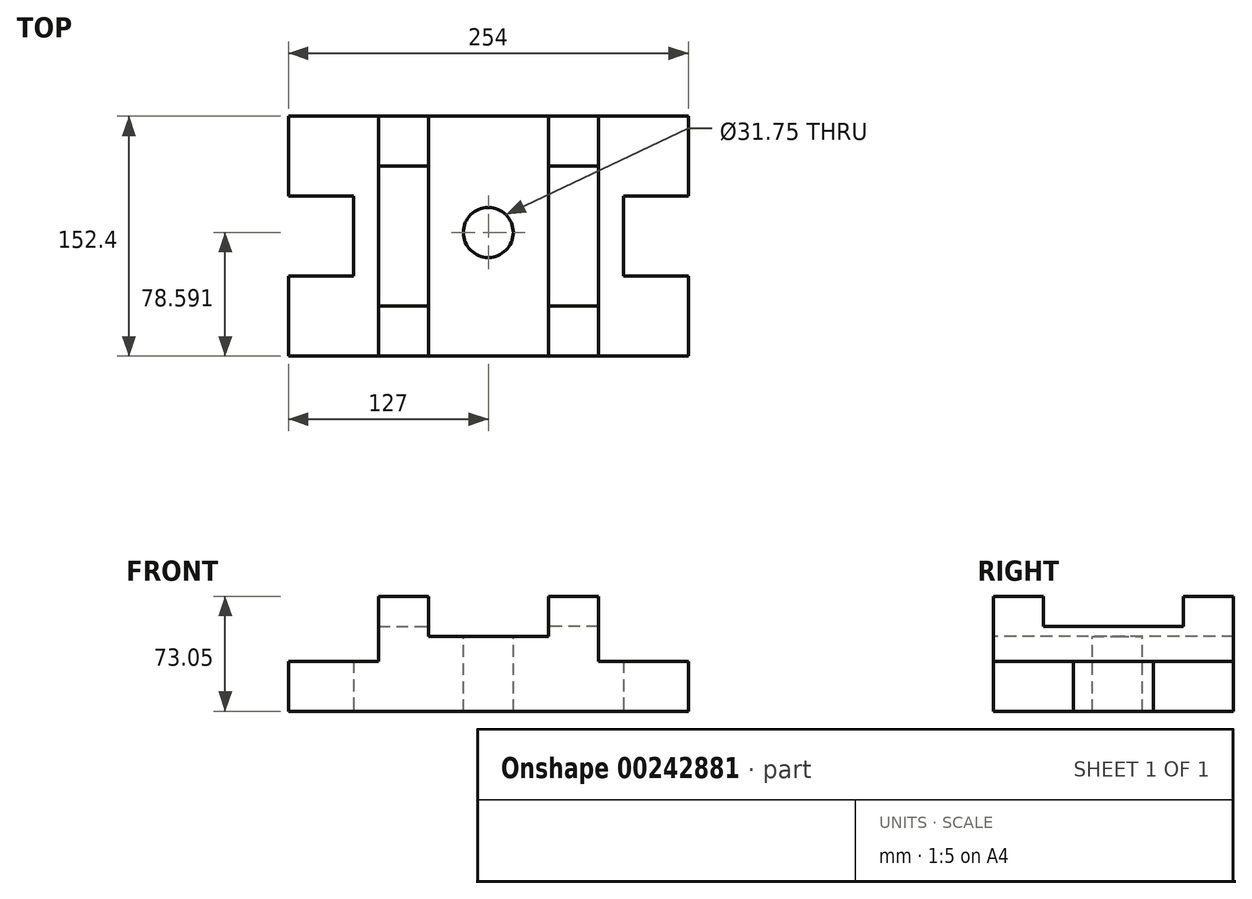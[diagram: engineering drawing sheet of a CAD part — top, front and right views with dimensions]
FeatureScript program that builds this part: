
annotation { "Feature Type Name" : "Feature", "Feature Type Description" : "" }
export const myFeature = defineFeature(function(context is Context, id is Id, definition is map)
    precondition{}
    {
        {
            var Q0;
            Q0=qCreatedBy(makeId("Top.planeOp"),FACE);
            var sketch = newSketch(context, id + "F0", { "sketchPlane" : qUnion([Q0])});
            skLineSegment(sketch, "E0.bottom", {"start": v(127, -76.2) * mm, "end": v(-127, -76.2) * mm});
            skLineSegment(sketch, "E0.top", {"start": v(127, 76.2) * mm, "end": v(-127, 76.2) * mm});
            skLineSegment(sketch, "E0.left", {"start": v(127, -76.2) * mm, "end": v(127, -25.4) * mm});
            skLineSegment(sketch, "E0.right", {"start": v(-127, -76.2) * mm, "end": v(-127, -25.4) * mm});
            skPoint(sketch, "E0.middle", {"position": v(0, 0) * mm});
            skLineSegment(sketch, "E1", {"start": v(127, 76.2) * mm, "end": v(127, 25.4) * mm});
            skLineSegment(sketch, "E2", {"start": v(127, 25.4) * mm, "end": v(85.72, 25.4) * mm});
            skLineSegment(sketch, "E3", {"start": v(127, -25.4) * mm, "end": v(85.72, -25.4) * mm});
            skLineSegment(sketch, "E4", {"start": v(85.72, 25.4) * mm, "end": v(85.72, -25.4) * mm});
            skLineSegment(sketch, "E5", {"start": v(-127, 25.4) * mm, "end": v(-85.72, 25.4) * mm});
            skLineSegment(sketch, "E6", {"start": v(-85.72, 25.4) * mm, "end": v(-85.72, -25.4) * mm});
            skLineSegment(sketch, "E7.trimOffspring", {"start": v(-127, 25.4) * mm, "end": v(-127, 76.2) * mm});
            skLineSegment(sketch, "E8.trimOffspring", {"start": v(127, 25.4) * mm, "end": v(127, 76.2) * mm});
            skLineSegment(sketch, "E9.trimOffspring", {"start": v(-85.72, 25.4) * mm, "end": v(-127, 25.4) * mm});
            skLineSegment(sketch, "E10.trimOffspring", {"start": v(-85.72, -25.4) * mm, "end": v(-127, -25.4) * mm});
            skSolve(sketch);
        }
        {
            var Q0;
            Q0 = qSketchRegion(id + "F0", true);
            extrude(context, id + "F1", {"entities" : qUnion([Q0]), "depth" : 31.75 * mm});
        }
        {
            var Q0;
            Q0=makeQuery(id+"F1.opExtrude","CAP_FACE",FACE,{"disambiguationData":[OSD([sQuery(id+"F0.wireOp",EDGE,"E0.bottom"),sQuery(id+"F0.wireOp",EDGE,"E0.top"),sQuery(id+"F0.wireOp",EDGE,"E0.right"),sQuery(id+"F0.wireOp",EDGE,"E0.left"),sQuery(id+"F0.wireOp",EDGE,"E3"),sQuery(id+"F0.wireOp",EDGE,"E2"),sQuery(id+"F0.wireOp",EDGE,"E4"),sQuery(id+"F0.wireOp",EDGE,"E6"),sQuery(id+"F0.wireOp",EDGE,"E7.trimOffspring"),sQuery(id+"F0.wireOp",EDGE,"E8.trimOffspring"),sQuery(id+"F0.wireOp",EDGE,"E9.trimOffspring"),sQuery(id+"F0.wireOp",EDGE,"E10.trimOffspring")])],"isStart":true});
            var sketch = newSketch(context, id + "F2", { "sketchPlane" : qUnion([Q0])});
            skLineSegment(sketch, "E11", {"start": v(127, 76.2) * mm, "end": v(69.85, 76.2) * mm});
            skLineSegment(sketch, "E12", {"start": v(-127, 76.2) * mm, "end": v(-69.85, 76.2) * mm});
            skLineSegment(sketch, "E13", {"start": v(-69.85, 76.2) * mm, "end": v(-69.85, -76.2) * mm});
            skLineSegment(sketch, "E14", {"start": v(69.85, 76.2) * mm, "end": v(69.85, -76.2) * mm});
            skSolve(sketch);
        }
        {
            var Q0;
            Q0=makeQuery(id+"F1.opExtrude","CAP_FACE",FACE,{"disambiguationData":[OSD([sQuery(id+"F0.wireOp",EDGE,"E0.bottom"),sQuery(id+"F0.wireOp",EDGE,"E0.top"),sQuery(id+"F0.wireOp",EDGE,"E0.right"),sQuery(id+"F0.wireOp",EDGE,"E0.left"),sQuery(id+"F0.wireOp",EDGE,"E3"),sQuery(id+"F0.wireOp",EDGE,"E2"),sQuery(id+"F0.wireOp",EDGE,"E4"),sQuery(id+"F0.wireOp",EDGE,"E6"),sQuery(id+"F0.wireOp",EDGE,"E7.trimOffspring"),sQuery(id+"F0.wireOp",EDGE,"E8.trimOffspring"),sQuery(id+"F0.wireOp",EDGE,"E9.trimOffspring"),sQuery(id+"F0.wireOp",EDGE,"E10.trimOffspring")])],"isStart":false});
            var sketch = newSketch(context, id + "F3", { "sketchPlane" : qUnion([Q0])});
            skLineSegment(sketch, "E15", {"start": v(-69.85, 76.2) * mm, "end": v(-38.1, 76.2) * mm});
            skLineSegment(sketch, "E16", {"start": v(69.85, 76.2) * mm, "end": v(38.1, 76.2) * mm});
            skLineSegment(sketch, "E17", {"start": v(-69.85, 76.2) * mm, "end": v(-69.85, 44.45) * mm});
            skLineSegment(sketch, "E18", {"start": v(69.85, 76.2) * mm, "end": v(69.85, 44.45) * mm});
            skLineSegment(sketch, "E19", {"start": v(38.1, 76.2) * mm, "end": v(38.1, 44.45) * mm});
            skLineSegment(sketch, "E20", {"start": v(38.1, 44.45) * mm, "end": v(69.85, 44.45) * mm});
            skLineSegment(sketch, "E21", {"start": v(-69.85, 44.45) * mm, "end": v(-38.1, 44.45) * mm});
            skLineSegment(sketch, "E22", {"start": v(-38.1, 44.45) * mm, "end": v(-38.1, 76.2) * mm});
            skLineSegment(sketch, "E23", {"start": v(-69.85, -76.2) * mm, "end": v(-69.85, -44.45) * mm});
            skLineSegment(sketch, "E24", {"start": v(-69.85, -44.45) * mm, "end": v(-38.1, -44.45) * mm});
            skLineSegment(sketch, "E25", {"start": v(-38.1, -44.45) * mm, "end": v(-38.1, -76.2) * mm});
            skLineSegment(sketch, "E26", {"start": v(69.85, -76.2) * mm, "end": v(38.1, -76.2) * mm});
            skLineSegment(sketch, "E27", {"start": v(38.1, -76.2) * mm, "end": v(38.1, -44.45) * mm});
            skLineSegment(sketch, "E28", {"start": v(38.1, -44.45) * mm, "end": v(69.85, -44.45) * mm});
            skLineSegment(sketch, "E29", {"start": v(38.1, 44.45) * mm, "end": v(38.1, -44.45) * mm});
            skLineSegment(sketch, "E30", {"start": v(-38.1, 44.45) * mm, "end": v(-38.1, -44.45) * mm});
            skLineSegment(sketch, "E31", {"start": v(69.85, 44.45) * mm, "end": v(69.85, -44.45) * mm});
            skLineSegment(sketch, "E32", {"start": v(-69.85, 44.45) * mm, "end": v(-69.85, -44.45) * mm});
            skLineSegment(sketch, "E33", {"start": v(69.85, -44.45) * mm, "end": v(69.85, -76.2) * mm});
            skSolve(sketch);
        }
        {
            var Q0;
            Q0=makeQuery(id+"F3.imprint","IMPRINT",FACE,{"disambiguationData":[TD([[makeQuery(id+"F3.imprint","IMPRINT",EDGE,{"derivedFrom":sQuery(id+"F3.wireOp",EDGE,"E15")}),1.0]])]});
            var Q1;
            Q1=makeQuery(id+"F3.imprint","IMPRINT",FACE,{"disambiguationData":[TD([[makeQuery(id+"F3.imprint","IMPRINT",EDGE,{"derivedFrom":sQuery(id+"F3.wireOp",EDGE,"E21")}),-1.0]])]});
            var Q2;
            {var subQ0=sQuery(id+"F3.wireOp",EDGE,"E23");Q2=makeQuery(id+"F3.imprint","IMPRINT",FACE,{"disambiguationData":[TD([[makeQuery(id+"F3.imprint","IMPRINT",EDGE,{"derivedFrom":subQ0}),-1.0]])]});}
            var Q3;
            Q3=makeQuery(id+"F3.imprint","IMPRINT",FACE,{"disambiguationData":[TD([[makeQuery(id+"F3.imprint","IMPRINT",EDGE,{"derivedFrom":sQuery(id+"F3.wireOp",EDGE,"E26")}),-1.0]])]});
            var Q4;
            Q4=makeQuery(id+"F3.imprint","IMPRINT",FACE,{"disambiguationData":[TD([[makeQuery(id+"F3.imprint","IMPRINT",EDGE,{"derivedFrom":sQuery(id+"F3.wireOp",EDGE,"E20")}),-1.0]])]});
            var Q5;
            Q5=makeQuery(id+"F3.imprint","IMPRINT",FACE,{"disambiguationData":[TD([[makeQuery(id+"F3.imprint","IMPRINT",EDGE,{"derivedFrom":sQuery(id+"F3.wireOp",EDGE,"E16")}),1.0]])]});
            var Q6;
            {var subQ3=sQuery(id+"F3.wireOp",EDGE,"E19");Q6=makeQuery(id+"F3.imprint","IMPRINT",FACE,{"disambiguationData":[TD([[makeQuery(id+"F3.imprint","IMPRINT",EDGE,{"derivedFrom":subQ3}),-1.0]])]});}
            extrude(context, id + "F4", {"entities" : qUnion([Q0, Q1, Q2, Q3, Q4, Q5, Q6]), "operationType" : NewBodyOperationType.ADD, "depth" : 22.22 * mm});
        }
        {
            var Q0;
            Q0=makeQuery(id+"F4.opExtrude","CAP_FACE",FACE,{"disambiguationData":[OSD([sQuery(id+"F0.wireOp",EDGE,"E0.bottom"),sQuery(id+"F3.wireOp",EDGE,"E15"),sQuery(id+"F3.wireOp",EDGE,"E17"),sQuery(id+"F3.wireOp",EDGE,"E22"),sQuery(id+"F3.wireOp",EDGE,"E23"),sQuery(id+"F3.wireOp",EDGE,"E25"),sQuery(id+"F3.wireOp",EDGE,"E30"),sQuery(id+"F3.wireOp",EDGE,"E32")])],"isStart":false});
            var Q1;
            Q1=makeQuery(id+"F4.opExtrude","CAP_FACE",FACE,{"disambiguationData":[OSD([sQuery(id+"F3.wireOp",EDGE,"E16"),sQuery(id+"F3.wireOp",EDGE,"E18"),sQuery(id+"F3.wireOp",EDGE,"E19"),sQuery(id+"F3.wireOp",EDGE,"E26"),sQuery(id+"F3.wireOp",EDGE,"E27"),sQuery(id+"F3.wireOp",EDGE,"E29"),sQuery(id+"F3.wireOp",EDGE,"E31"),sQuery(id+"F3.wireOp",EDGE,"E33")])],"isStart":false});
            extrude(context, id + "F5", {"entities" : qUnion([Q0, Q1]), "operationType" : NewBodyOperationType.ADD, "depth" : 19.05 * mm});
        }
        {
            var Q0;
            Q0=makeQuery(id+"F5.opExtrude","CAP_FACE",FACE,{"disambiguationData":[OSD([sQuery(id+"F0.wireOp",EDGE,"E0.bottom"),sQuery(id+"F0.wireOp",EDGE,"E0.top"),sQuery(id+"F3.wireOp",EDGE,"E15"),sQuery(id+"F3.wireOp",EDGE,"E16"),sQuery(id+"F3.wireOp",EDGE,"E17"),sQuery(id+"F3.wireOp",EDGE,"E18"),sQuery(id+"F3.wireOp",EDGE,"E23"),sQuery(id+"F3.wireOp",EDGE,"E26"),sQuery(id+"F3.wireOp",EDGE,"E31"),sQuery(id+"F3.wireOp",EDGE,"E32"),sQuery(id+"F3.wireOp",EDGE,"E33")])],"isStart":false});
            var sketch = newSketch(context, id + "F6", { "sketchPlane" : qUnion([Q0])});
            skLineSegment(sketch, "E34", {"start": v(-69.85, 76.2) * mm, "end": v(-38.1, 76.2) * mm});
            skLineSegment(sketch, "E35", {"start": v(-38.1, 76.2) * mm, "end": v(-38.1, -76.2) * mm});
            skLineSegment(sketch, "E36", {"start": v(69.85, 76.2) * mm, "end": v(38.1, 76.2) * mm});
            skLineSegment(sketch, "E37", {"start": v(38.1, 76.2) * mm, "end": v(38.1, -76.2) * mm});
            skSolve(sketch);
        }
        {
            var Q0;
            Q0 = qSketchRegion(id + "F6", true);
            var Q1;
            Q1=makeQuery(id+"F6.imprint","IMPRINT",FACE,{"disambiguationData":[TD([[makeQuery(id+"F6.imprint","IMPRINT",EDGE,{"derivedFrom":sQuery(id+"F6.wireOp",EDGE,"E34")}),1.0]])]});
            var Q2;
            Q2=makeQuery(id+"F6.imprint","IMPRINT",FACE,{"disambiguationData":[TD([[makeQuery(id+"F6.imprint","IMPRINT",EDGE,{"derivedFrom":sQuery(id+"F6.wireOp",EDGE,"E36")}),1.0]])]});
            extrude(context, id + "F7", {"entities" : qUnion([Q0, Q1, Q2]), "operationType" : NewBodyOperationType.ADD, "depth" : 3 / 101.6 * mm});
        }
        {
            var Q0;
            Q0=makeQuery(id+"F5.opExtrude","CAP_FACE",FACE,{"disambiguationData":[OSD([sQuery(id+"F0.wireOp",EDGE,"E0.bottom"),sQuery(id+"F0.wireOp",EDGE,"E0.top"),sQuery(id+"F3.wireOp",EDGE,"E15"),sQuery(id+"F3.wireOp",EDGE,"E16"),sQuery(id+"F3.wireOp",EDGE,"E17"),sQuery(id+"F3.wireOp",EDGE,"E18"),sQuery(id+"F3.wireOp",EDGE,"E23"),sQuery(id+"F3.wireOp",EDGE,"E26"),sQuery(id+"F3.wireOp",EDGE,"E31"),sQuery(id+"F3.wireOp",EDGE,"E32"),sQuery(id+"F3.wireOp",EDGE,"E33")])],"isStart":false});
            extrude(context, id + "F8", {"entities" : qUnion([Q0]), "operationType" : NewBodyOperationType.REMOVE, "oppositeDirection" : true, "depth" : 25.4 * mm});
        }
        {
            var Q0;
            Q0=makeQuery(id+"F7.opExtrude","CAP_FACE",FACE,{"disambiguationData":[OSD([sQuery(id+"F0.wireOp",EDGE,"E0.bottom"),sQuery(id+"F3.wireOp",EDGE,"E18"),sQuery(id+"F3.wireOp",EDGE,"E26"),sQuery(id+"F3.wireOp",EDGE,"E31"),sQuery(id+"F3.wireOp",EDGE,"E33"),sQuery(id+"F6.wireOp",EDGE,"E36"),sQuery(id+"F6.wireOp",EDGE,"E37")])],"isStart":false});
            var sketch = newSketch(context, id + "F9", { "sketchPlane" : qUnion([Q0])});
            skLineSegment(sketch, "E38", {"start": v(69.85, 76.2) * mm, "end": v(69.85, 44.45) * mm});
            skLineSegment(sketch, "E39", {"start": v(69.85, 44.45) * mm, "end": v(38.1, 44.45) * mm});
            skLineSegment(sketch, "E40", {"start": v(69.85, -76.2) * mm, "end": v(69.85, -44.45) * mm});
            skLineSegment(sketch, "E41", {"start": v(69.85, -44.45) * mm, "end": v(38.1, -44.45) * mm});
            skLineSegment(sketch, "E42", {"start": v(69.85, 76.2) * mm, "end": v(38.1, 76.2) * mm});
            skLineSegment(sketch, "E43", {"start": v(38.1, 44.45) * mm, "end": v(38.1, 76.2) * mm});
            skLineSegment(sketch, "E44", {"start": v(38.1, -44.45) * mm, "end": v(38.1, -76.2) * mm});
            skLineSegment(sketch, "E45", {"start": v(38.1, -76.2) * mm, "end": v(69.85, -76.2) * mm});
            skSolve(sketch);
        }
        {
            var Q0;
            Q0=makeQuery(id+"F7.opExtrude","CAP_FACE",FACE,{"disambiguationData":[OSD([sQuery(id+"F0.wireOp",EDGE,"E0.bottom"),sQuery(id+"F3.wireOp",EDGE,"E17"),sQuery(id+"F3.wireOp",EDGE,"E23"),sQuery(id+"F3.wireOp",EDGE,"E26"),sQuery(id+"F3.wireOp",EDGE,"E32"),sQuery(id+"F6.wireOp",EDGE,"E34"),sQuery(id+"F6.wireOp",EDGE,"E35")])],"isStart":false});
            var sketch = newSketch(context, id + "F10", { "sketchPlane" : qUnion([Q0])});
            skLineSegment(sketch, "E46", {"start": v(-69.85, 76.2) * mm, "end": v(-69.85, 44.45) * mm});
            skLineSegment(sketch, "E47", {"start": v(-69.85, 44.45) * mm, "end": v(-38.1, 44.45) * mm});
            skLineSegment(sketch, "E48", {"start": v(-38.1, 44.45) * mm, "end": v(-38.1, 76.2) * mm});
            skLineSegment(sketch, "E49", {"start": v(-38.1, 76.2) * mm, "end": v(-69.85, 76.2) * mm});
            skLineSegment(sketch, "E50", {"start": v(-69.85, 76.2) * mm, "end": v(-38.1, 76.2) * mm});
            skLineSegment(sketch, "E51", {"start": v(-69.85, -76.2) * mm, "end": v(-38.1, -76.2) * mm});
            skLineSegment(sketch, "E52", {"start": v(-38.1, -76.2) * mm, "end": v(-38.1, -44.45) * mm});
            skLineSegment(sketch, "E53", {"start": v(-38.1, -44.45) * mm, "end": v(-69.85, -44.45) * mm});
            skLineSegment(sketch, "E54", {"start": v(-69.85, -44.45) * mm, "end": v(-69.85, -76.2) * mm});
            skSolve(sketch);
        }
        {
            var Q0;
            {var subQ0=sQuery(id+"F10.wireOp",EDGE,"E47");Q0=makeQuery(id+"F10.imprint","IMPRINT",FACE,{"disambiguationData":[TD([[makeQuery(id+"F10.imprint","IMPRINT",EDGE,{"derivedFrom":subQ0}),-1.0]])]});}
            extrude(context, id + "F11", {"entities" : qUnion([Q0]), "operationType" : NewBodyOperationType.REMOVE, "oppositeDirection" : true, "depth" : 19.05 * mm});
        }
        {
            var Q0;
            {var subQ0=sQuery(id+"F9.wireOp",EDGE,"E39");Q0=makeQuery(id+"F9.imprint","IMPRINT",FACE,{"disambiguationData":[TD([[makeQuery(id+"F9.imprint","IMPRINT",EDGE,{"derivedFrom":subQ0}),1.0]])]});}
            extrude(context, id + "F12", {"entities" : qUnion([Q0]), "operationType" : NewBodyOperationType.REMOVE, "oppositeDirection" : true, "depth" : 19.05 * mm});
        }
        {
            var Q0;
            Q0=makeQuery(id+"F8.boolean.opBoolean","COPY",FACE,{"derivedFrom":makeQuery(id+"F8.opExtrude","CAP_FACE",FACE,{"disambiguationData":[OSD([sQuery(id+"F0.wireOp",EDGE,"E0.bottom"),sQuery(id+"F0.wireOp",EDGE,"E0.top"),sQuery(id+"F3.wireOp",EDGE,"E15"),sQuery(id+"F3.wireOp",EDGE,"E16"),sQuery(id+"F3.wireOp",EDGE,"E17"),sQuery(id+"F3.wireOp",EDGE,"E18"),sQuery(id+"F3.wireOp",EDGE,"E23"),sQuery(id+"F3.wireOp",EDGE,"E26"),sQuery(id+"F3.wireOp",EDGE,"E31"),sQuery(id+"F3.wireOp",EDGE,"E32"),sQuery(id+"F3.wireOp",EDGE,"E33")])],"isStart":false})});
            var sketch = newSketch(context, id + "F13", { "sketchPlane" : qUnion([Q0])});
            skCircle(sketch, "E55", {"center": v(0, 2.4) * mm, "radius": 15.88 * mm});
            skSolve(sketch);
        }
        {
            var Q0;
            Q0=makeQuery(id+"F13.imprint","IMPRINT",FACE,{"disambiguationData":[TD([[makeQuery(id+"F13.imprint","IMPRINT",EDGE,{"derivedFrom":sQuery(id+"F13.wireOp",EDGE,"E55")}),1.0]])]});
            extrude(context, id + "F14", {"entities" : qUnion([Q0]), "operationType" : NewBodyOperationType.REMOVE, "oppositeDirection" : true, "depth" : 53.97 * mm});
        }
    });
